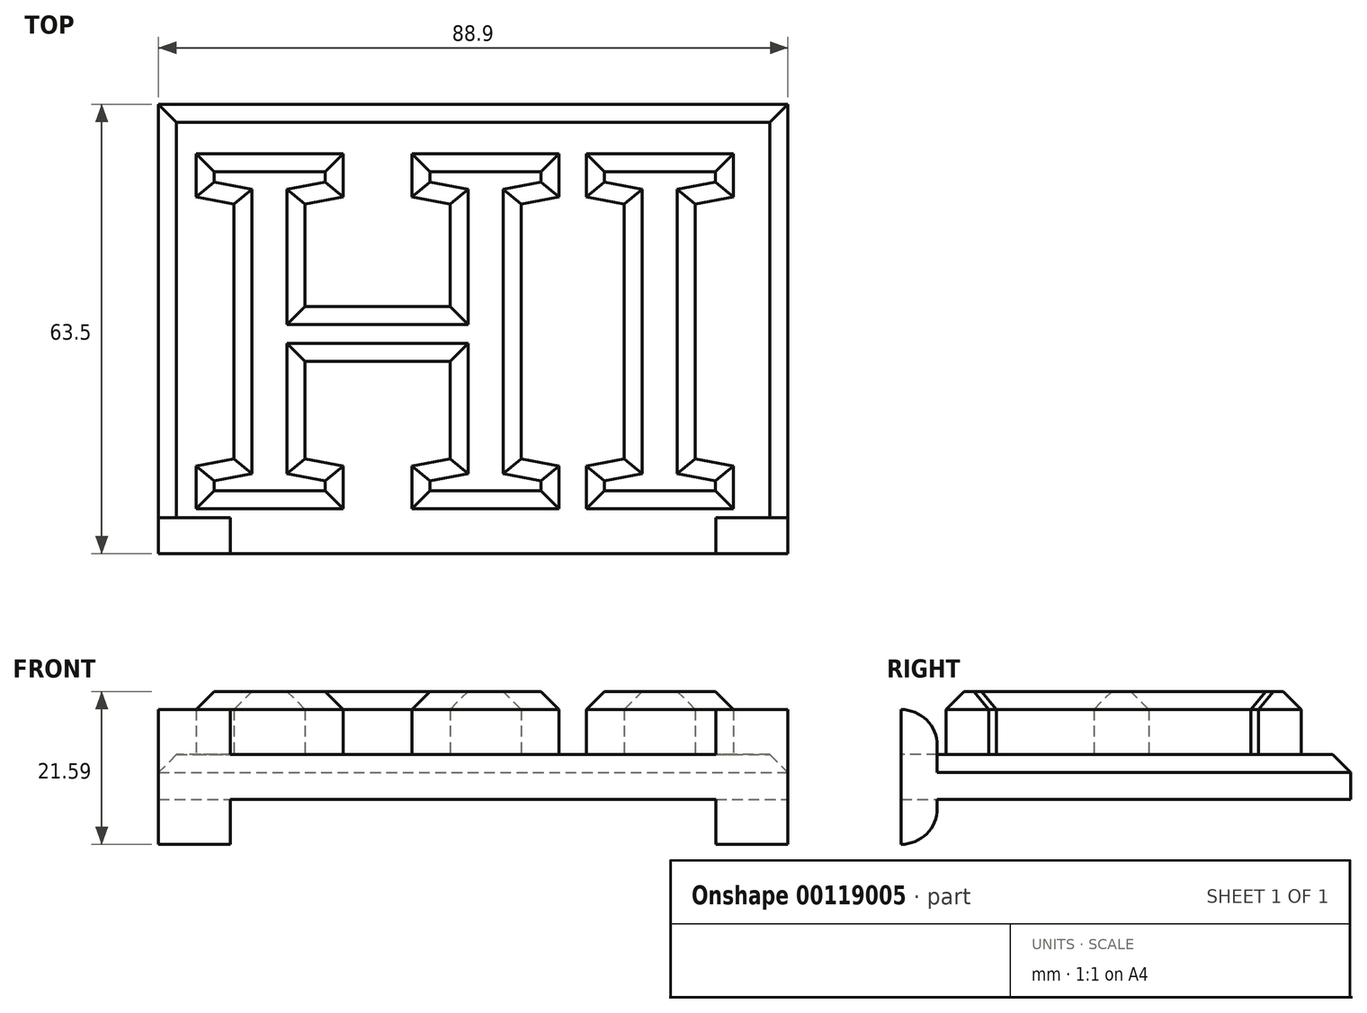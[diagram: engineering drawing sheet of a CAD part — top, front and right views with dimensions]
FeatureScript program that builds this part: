
annotation { "Feature Type Name" : "Feature", "Feature Type Description" : "" }
export const myFeature = defineFeature(function(context is Context, id is Id, definition is map)
    precondition{}
    {
        {
            var Q0;
            Q0=qCreatedBy(makeId("Top.planeOp"),FACE);
            var sketch = newSketch(context, id + "F0", { "sketchPlane" : qUnion([Q0])});
            skText(sketch, "E0", { "text": "HI", "fontName": "RobotoSlab-Bold.ttf"});
            const initialGuessF0  = {"E0": [-0.04107, -0.0254, 1, 0, 0.0508]};
            skSetInitialGuess(sketch, initialGuessF0);
            skSolve(sketch);
        }
        {
            var Q0;
            Q0 = qSketchRegion(id + "F0", true);
            extrude(context, id + "F1", {"entities" : qUnion([Q0]), "depth" : 8.9 * mm});
        }
        {
            var Q0;
            Q0=qCreatedBy(makeId("Top.planeOp"),FACE);
            var sketch = newSketch(context, id + "F2", { "sketchPlane" : qUnion([Q0])});
            skLineSegment(sketch, "E1.bottom", {"start": v(44.45, -31.75) * mm, "end": v(-44.45, -31.75) * mm});
            skLineSegment(sketch, "E1.top", {"start": v(44.45, 31.75) * mm, "end": v(-44.45, 31.75) * mm});
            skLineSegment(sketch, "E1.left", {"start": v(44.45, -31.75) * mm, "end": v(44.45, 31.75) * mm});
            skLineSegment(sketch, "E1.right", {"start": v(-44.45, -31.75) * mm, "end": v(-44.45, 31.75) * mm});
            skPoint(sketch, "E1.middle", {"position": v(0, 0) * mm});
            skSolve(sketch);
        }
        {
            var Q0;
            Q0=makeQuery(id+"F2.imprint","IMPRINT",FACE,{"disambiguationData":[TD([[makeQuery(id+"F2.imprint","IMPRINT",EDGE,{"derivedFrom":sQuery(id+"F2.wireOp",EDGE,"E1.bottom")}),-1.0]])]});
            extrude(context, id + "F3", {"entities" : qUnion([Q0]), "oppositeDirection" : true, "depth" : 6.35 * mm});
        }
        {
            var Q0;
            Q0=makeQuery(id+"F3.opExtrude","SWEPT_FACE",FACE,{"disambiguationData":[OSD([sQuery(id+"F2.wireOp",EDGE,"E1.bottom")])]});
            var sketch = newSketch(context, id + "F4", { "sketchPlane" : qUnion([Q0])});
            skLineSegment(sketch, "E2.bottom", {"start": v(-44.45, 6.35) * mm, "end": v(-34.3, 6.35) * mm});
            skLineSegment(sketch, "E2.top", {"start": v(-44.45, -12.7) * mm, "end": v(-34.3, -12.7) * mm});
            skLineSegment(sketch, "E2.left", {"start": v(-44.45, 6.35) * mm, "end": v(-44.45, -12.7) * mm});
            skLineSegment(sketch, "E2.right", {"start": v(-34.3, 6.35) * mm, "end": v(-34.3, -12.7) * mm});
            skLineSegment(sketch, "E3.bottom", {"start": v(44.45, -12.7) * mm, "end": v(34.29, -12.7) * mm});
            skLineSegment(sketch, "E3.top", {"start": v(44.45, 6.35) * mm, "end": v(34.29, 6.35) * mm});
            skLineSegment(sketch, "E3.left", {"start": v(44.45, -12.7) * mm, "end": v(44.45, 6.35) * mm});
            skLineSegment(sketch, "E3.right", {"start": v(34.29, -12.7) * mm, "end": v(34.29, 6.35) * mm});
            skSolve(sketch);
        }
        {
            var Q0;
            Q0 = qSketchRegion(id + "F4", true);
            extrude(context, id + "F5", {"entities" : qUnion([Q0]), "operationType" : NewBodyOperationType.ADD, "oppositeDirection" : true, "depth" : 5.08 * mm});
        }
        {
            var Q0;
            Q0=makeQuery(id+"F1.opExtrude","CAP_EDGE",EDGE,{"disambiguationData":[OSD([sQuery(id+"F0.wireOp",EDGE,"E0.sketch_text.stroke-28")])],"isStart":false});
            var Q1;
            Q1=makeQuery(id+"F1.opExtrude","CAP_EDGE",EDGE,{"disambiguationData":[OSD([sQuery(id+"F0.wireOp",EDGE,"E0.sketch_text.stroke-4")])],"isStart":false});
            var Q2;
            Q2=makeQuery(id+"F1.opExtrude","CAP_EDGE",EDGE,{"disambiguationData":[OSD([sQuery(id+"F0.wireOp",EDGE,"E0.sketch_text.stroke-5")])],"isStart":false});
            var Q3;
            Q3=makeQuery(id+"F1.opExtrude","CAP_FACE",FACE,{"disambiguationData":[OSD([sQuery(id+"F0.wireOp",EDGE,"E0.sketch_text.stroke-0"),sQuery(id+"F0.wireOp",EDGE,"E0.sketch_text.stroke-1"),sQuery(id+"F0.wireOp",EDGE,"E0.sketch_text.stroke-2"),sQuery(id+"F0.wireOp",EDGE,"E0.sketch_text.stroke-3"),sQuery(id+"F0.wireOp",EDGE,"E0.sketch_text.stroke-4"),sQuery(id+"F0.wireOp",EDGE,"E0.sketch_text.stroke-5"),sQuery(id+"F0.wireOp",EDGE,"E0.sketch_text.stroke-6"),sQuery(id+"F0.wireOp",EDGE,"E0.sketch_text.stroke-7"),sQuery(id+"F0.wireOp",EDGE,"E0.sketch_text.stroke-8"),sQuery(id+"F0.wireOp",EDGE,"E0.sketch_text.stroke-9"),sQuery(id+"F0.wireOp",EDGE,"E0.sketch_text.stroke-10"),sQuery(id+"F0.wireOp",EDGE,"E0.sketch_text.stroke-11"),sQuery(id+"F0.wireOp",EDGE,"E0.sketch_text.stroke-12"),sQuery(id+"F0.wireOp",EDGE,"E0.sketch_text.stroke-13"),sQuery(id+"F0.wireOp",EDGE,"E0.sketch_text.stroke-14"),sQuery(id+"F0.wireOp",EDGE,"E0.sketch_text.stroke-15"),sQuery(id+"F0.wireOp",EDGE,"E0.sketch_text.stroke-16"),sQuery(id+"F0.wireOp",EDGE,"E0.sketch_text.stroke-17"),sQuery(id+"F0.wireOp",EDGE,"E0.sketch_text.stroke-18"),sQuery(id+"F0.wireOp",EDGE,"E0.sketch_text.stroke-19"),sQuery(id+"F0.wireOp",EDGE,"E0.sketch_text.stroke-20"),sQuery(id+"F0.wireOp",EDGE,"E0.sketch_text.stroke-21"),sQuery(id+"F0.wireOp",EDGE,"E0.sketch_text.stroke-22"),sQuery(id+"F0.wireOp",EDGE,"E0.sketch_text.stroke-23"),sQuery(id+"F0.wireOp",EDGE,"E0.sketch_text.stroke-24"),sQuery(id+"F0.wireOp",EDGE,"E0.sketch_text.stroke-25"),sQuery(id+"F0.wireOp",EDGE,"E0.sketch_text.stroke-26"),sQuery(id+"F0.wireOp",EDGE,"E0.sketch_text.stroke-27"),sQuery(id+"F0.wireOp",EDGE,"E0.sketch_text.stroke-28"),sQuery(id+"F0.wireOp",EDGE,"E0.sketch_text.stroke-29")])],"isStart":false});
            var Q4;
            Q4=makeQuery(id+"F1.opExtrude","CAP_EDGE",EDGE,{"disambiguationData":[OSD([sQuery(id+"F0.wireOp",EDGE,"E0.sketch_text.stroke-40")])],"isStart":false});
            var Q5;
            Q5=makeQuery(id+"F1.opExtrude","CAP_EDGE",EDGE,{"disambiguationData":[OSD([sQuery(id+"F0.wireOp",EDGE,"E0.sketch_text.stroke-37")])],"isStart":false});
            var Q6;
            Q6=makeQuery(id+"F1.opExtrude","CAP_EDGE",EDGE,{"disambiguationData":[OSD([sQuery(id+"F0.wireOp",EDGE,"E0.sketch_text.stroke-38")])],"isStart":false});
            var Q7;
            Q7=makeQuery(id+"F1.opExtrude","CAP_EDGE",EDGE,{"disambiguationData":[OSD([sQuery(id+"F0.wireOp",EDGE,"E0.sketch_text.stroke-39")])],"isStart":false});
            var Q8;
            Q8=makeQuery(id+"F1.opExtrude","CAP_EDGE",EDGE,{"disambiguationData":[OSD([sQuery(id+"F0.wireOp",EDGE,"E0.sketch_text.stroke-36")])],"isStart":false});
            var Q9;
            Q9=makeQuery(id+"F1.opExtrude","CAP_EDGE",EDGE,{"disambiguationData":[OSD([sQuery(id+"F0.wireOp",EDGE,"E0.sketch_text.stroke-35")])],"isStart":false});
            var Q10;
            Q10=makeQuery(id+"F1.opExtrude","CAP_EDGE",EDGE,{"disambiguationData":[OSD([sQuery(id+"F0.wireOp",EDGE,"E0.sketch_text.stroke-34")])],"isStart":false});
            var Q11;
            Q11=makeQuery(id+"F1.opExtrude","CAP_EDGE",EDGE,{"disambiguationData":[OSD([sQuery(id+"F0.wireOp",EDGE,"E0.sketch_text.stroke-33")])],"isStart":false});
            var Q12;
            Q12=makeQuery(id+"F1.opExtrude","CAP_EDGE",EDGE,{"disambiguationData":[OSD([sQuery(id+"F0.wireOp",EDGE,"E0.sketch_text.stroke-32")])],"isStart":false});
            var Q13;
            Q13=makeQuery(id+"F1.opExtrude","CAP_EDGE",EDGE,{"disambiguationData":[OSD([sQuery(id+"F0.wireOp",EDGE,"E0.sketch_text.stroke-31")])],"isStart":false});
            var Q14;
            Q14=makeQuery(id+"F1.opExtrude","CAP_EDGE",EDGE,{"disambiguationData":[OSD([sQuery(id+"F0.wireOp",EDGE,"E0.sketch_text.stroke-30")])],"isStart":false});
            var Q15;
            Q15=makeQuery(id+"F1.opExtrude","CAP_EDGE",EDGE,{"disambiguationData":[OSD([sQuery(id+"F0.wireOp",EDGE,"E0.sketch_text.stroke-41")])],"isStart":false});
            var Q16;
            Q16=makeQuery(id+"F3.opExtrude","CAP_EDGE",EDGE,{"disambiguationData":[OSD([sQuery(id+"F2.wireOp",EDGE,"E1.right")])],"isStart":true});
            var Q17;
            Q17=makeQuery(id+"F3.opExtrude","CAP_EDGE",EDGE,{"disambiguationData":[OSD([sQuery(id+"F2.wireOp",EDGE,"E1.top")])],"isStart":true});
            var Q18;
            Q18=makeQuery(id+"F3.opExtrude","CAP_EDGE",EDGE,{"disambiguationData":[OSD([sQuery(id+"F2.wireOp",EDGE,"E1.left")])],"isStart":true});
            chamfer(context, id + "F6", {"entities" : qUnion([Q0, Q1, Q2, Q3, Q4, Q5, Q6, Q7, Q8, Q9, Q10, Q11, Q12, Q13, Q14, Q15, Q16, Q17, Q18]), "width" : 2.54 * mm});
        }
        {
            var Q0;
            Q0=makeQuery(id+"F5.opExtrude","CAP_EDGE",EDGE,{"disambiguationData":[OSD([sQuery(id+"F4.wireOp",EDGE,"E3.bottom")])],"isStart":false});
            var Q1;
            Q1=makeQuery(id+"F5.opExtrude","CAP_EDGE",EDGE,{"disambiguationData":[OSD([sQuery(id+"F4.wireOp",EDGE,"E2.top")])],"isStart":false});
            var Q2;
            Q2=makeQuery(id+"F5.opExtrude","CAP_EDGE",EDGE,{"disambiguationData":[OSD([sQuery(id+"F4.wireOp",EDGE,"E3.top")])],"isStart":false});
            var Q3;
            Q3=makeQuery(id+"F5.opExtrude","CAP_EDGE",EDGE,{"disambiguationData":[OSD([sQuery(id+"F4.wireOp",EDGE,"E2.bottom")])],"isStart":false});
            fillet(context, id + "F7", {"entities" : qUnion([Q0, Q1, Q2, Q3]), "radius" : 5.08 * mm, "tangentPropagation" : true, "allowEdgeOverflow" : false});
        }
    });
